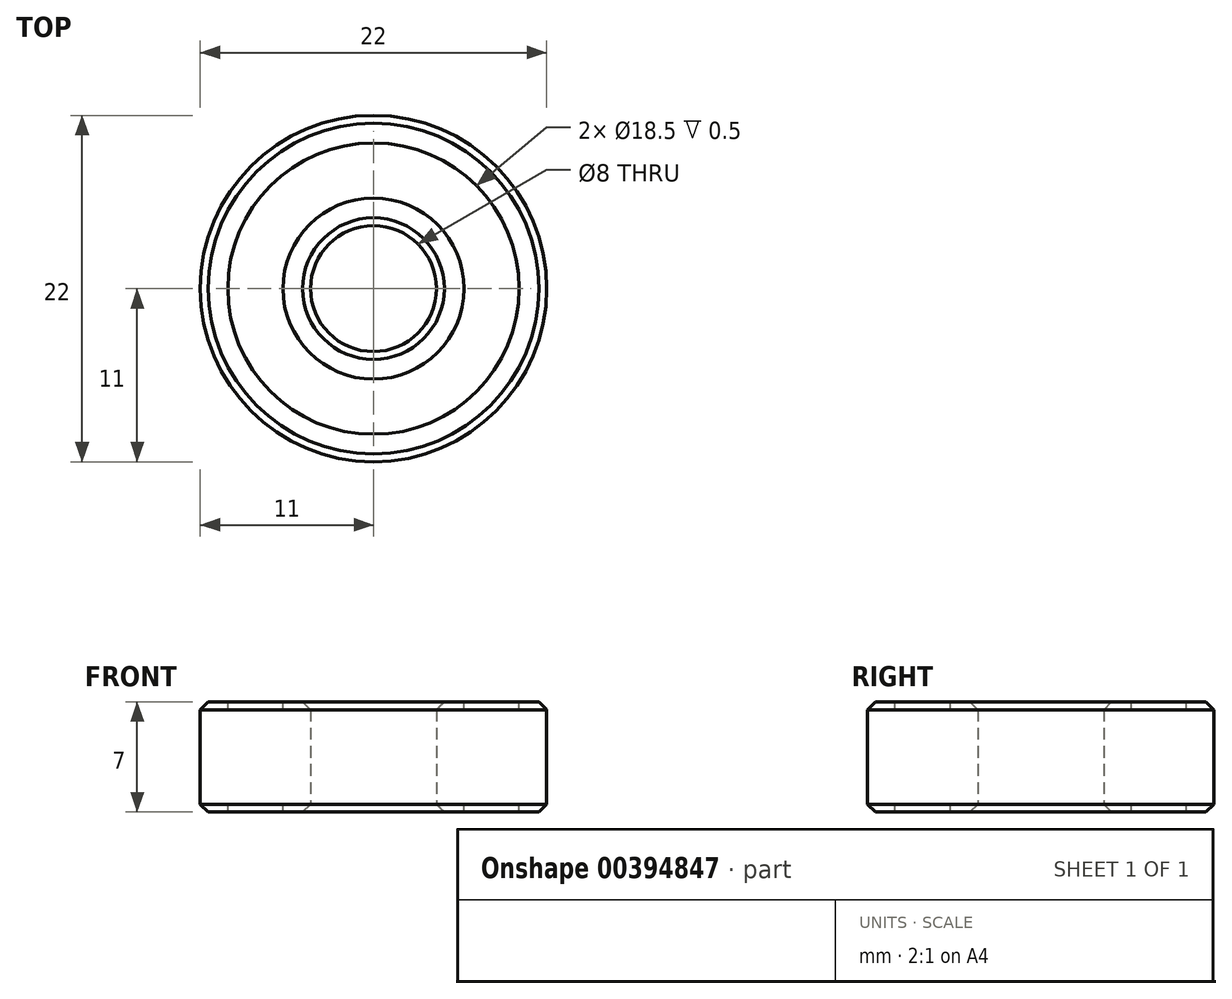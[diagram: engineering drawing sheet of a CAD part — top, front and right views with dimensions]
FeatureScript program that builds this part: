
annotation { "Feature Type Name" : "Feature", "Feature Type Description" : "" }
export const myFeature = defineFeature(function(context is Context, id is Id, definition is map)
    precondition{}
    {
        {
            var Q0;
            Q0=qCreatedBy(makeId("Top.planeOp"),FACE);
            var sketch = newSketch(context, id + "F0", { "sketchPlane" : qUnion([Q0])});
            skCircle(sketch, "E0", {"center": v(0, 0) * mm, "radius": 4 * mm});
            skCircle(sketch, "E1", {"center": v(0, 0) * mm, "radius": 11 * mm});
            skSolve(sketch);
        }
        {
            var Q0;
            Q0=makeQuery(id+"F0.imprint","IMPRINT",FACE,{"disambiguationData":[TD([[makeQuery(id+"F0.imprint","IMPRINT",EDGE,{"derivedFrom":sQuery(id+"F0.wireOp",EDGE,"E0")}),-1.0]])]});
            extrude(context, id + "F1", {"entities" : qUnion([Q0]), "depth" : 7 * mm, "symmetric" : true});
        }
        {
            var Q0;
            Q0=makeQuery(id+"F1.opExtrude","CAP_EDGE",EDGE,{"disambiguationData":[OSD([sQuery(id+"F0.wireOp",EDGE,"E1")])],"isStart":false});
            var Q1;
            Q1=makeQuery(id+"F1.opExtrude","CAP_EDGE",EDGE,{"disambiguationData":[OSD([sQuery(id+"F0.wireOp",EDGE,"E1")])],"isStart":true});
            var Q2;
            Q2=makeQuery(id+"F1.opExtrude","CAP_EDGE",EDGE,{"disambiguationData":[OSD([sQuery(id+"F0.wireOp",EDGE,"E0")])],"isStart":false});
            var Q3;
            Q3=makeQuery(id+"F1.opExtrude","CAP_EDGE",EDGE,{"disambiguationData":[OSD([sQuery(id+"F0.wireOp",EDGE,"E0")])],"isStart":true});
            chamfer(context, id + "F2", {"entities" : qUnion([Q0, Q1, Q2, Q3]), "width" : 0.5 * mm, "tangentPropagation" : true});
        }
        {
            var Q0;
            Q0=qCreatedBy(makeId("Right.planeOp"),FACE);
            var sketch = newSketch(context, id + "F3", { "sketchPlane" : qUnion([Q0])});
            skLineSegment(sketch, "E2.0", {"start": v(4.5, 3.5) * mm, "end": v(10.5, 3.5) * mm});
            skPoint(sketch, "E3.0.end.orphan", {"position": v(-4.5, 3.5) * mm});
            skPoint(sketch, "E3.0.start.orphan", {"position": v(4.5, 3.5) * mm});
            skPoint(sketch, "E4.orphan", {"position": v(-10.5, 3.5) * mm});
            skPoint(sketch, "E5.0.end.orphan", {"position": v(-10.5, -3.5) * mm});
            skPoint(sketch, "E5.0.start.orphan", {"position": v(10.5, -3.5) * mm});
            skLineSegment(sketch, "E6.bottom", {"start": v(5.75, 3) * mm, "end": v(9.25, 3) * mm});
            skLineSegment(sketch, "E6.top", {"start": v(5.75, 4) * mm, "end": v(9.25, 4) * mm});
            skLineSegment(sketch, "E6.left", {"start": v(5.75, 3) * mm, "end": v(5.75, 4) * mm});
            skLineSegment(sketch, "E6.right", {"start": v(9.25, 3) * mm, "end": v(9.25, 4) * mm});
            skPoint(sketch, "E6.middle", {"position": v(7.5, 3.5) * mm});
            skLineSegment(sketch, "E7", {"start": v(11, 3) * mm, "end": v(11, -3) * mm});
            skLineSegment(sketch, "E8.MirrorCS", {"start": v(5.75, -4) * mm, "end": v(9.25, -4) * mm});
            skLineSegment(sketch, "E9.MirrorCS", {"start": v(5.75, -3) * mm, "end": v(9.25, -3) * mm});
            skLineSegment(sketch, "E10.MirrorCS", {"start": v(5.75, -3) * mm, "end": v(5.75, -4) * mm});
            skLineSegment(sketch, "E11.MirrorCS", {"start": v(9.25, -3) * mm, "end": v(9.25, -4) * mm});
            skPoint(sketch, "E12.MirrorP", {"position": v(7.5, -3.5) * mm});
            skSolve(sketch);
        }
        {
            var Q0;
            Q0=qSketchRegion(id+"F3",true);
            var Q1;
            {var subQ0=sQuery(id+"F0.wireOp",EDGE,"E0");Q1=makeQuery(id+"F2.opChamfer","BLEND_EDGE",EDGE,{"blendedFrom":[makeQuery(id+"F1.opExtrude","CAP_EDGE",EDGE,{"disambiguationData":[OSD([subQ0])],"isStart":false}),makeQuery(id+"F1.opExtrude","CAP_FACE",FACE,{"disambiguationData":[OSD([subQ0,sQuery(id+"F0.wireOp",EDGE,"E1")])],"isStart":false})],"blendedInto":[makeQuery(id+"F1.opExtrude","CAP_FACE",FACE,{"disambiguationData":[OSD([subQ0,sQuery(id+"F0.wireOp",EDGE,"E1")])],"isStart":false})]});}
            revolve(context, id + "F4", {"operationType" : NewBodyOperationType.REMOVE, "entities" : qUnion([Q0]), "axis" : qUnion([Q1]), "revolveType" : RevolveType.FULL, "oppositeDirection" : true});
        }
    });
